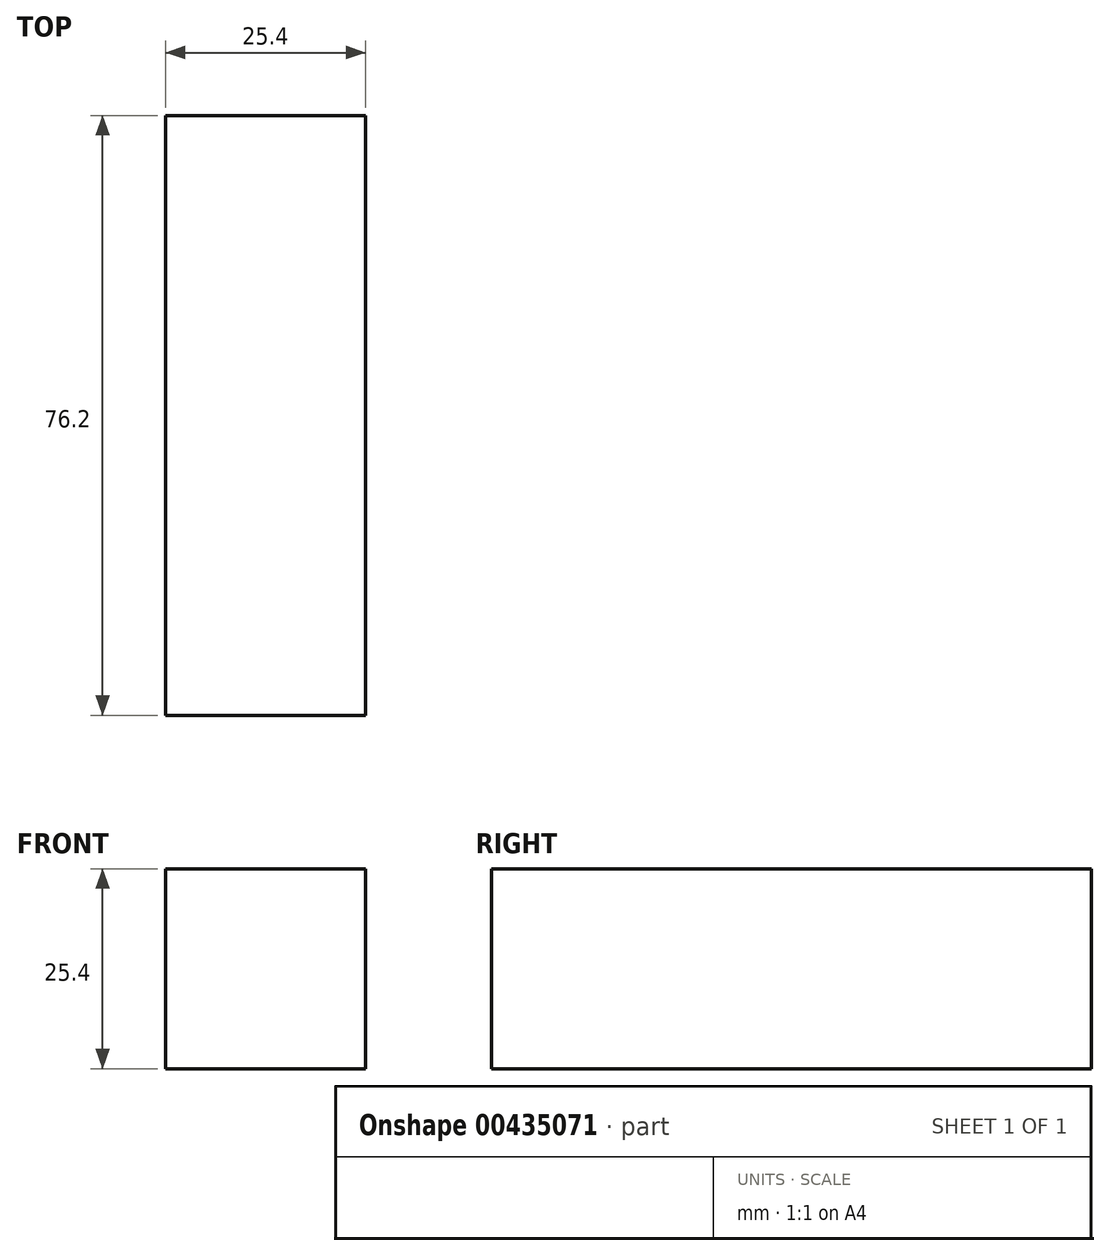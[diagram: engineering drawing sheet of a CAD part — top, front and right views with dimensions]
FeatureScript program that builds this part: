
annotation { "Feature Type Name" : "Feature", "Feature Type Description" : "" }
export const myFeature = defineFeature(function(context is Context, id is Id, definition is map)
    precondition{}
    {
        {
            var Q0;
            Q0=qCreatedBy(makeId("Front.planeOp"),FACE);
            var sketch = newSketch(context, id + "F0", { "sketchPlane" : qUnion([Q0])});
            skLineSegment(sketch, "E0.bottom", {"start": v(0, 0) * mm, "end": v(25.4, 0) * mm});
            skLineSegment(sketch, "E0.top", {"start": v(0, 25.4) * mm, "end": v(25.4, 25.4) * mm});
            skLineSegment(sketch, "E0.left", {"start": v(0, 0) * mm, "end": v(0, 25.4) * mm});
            skLineSegment(sketch, "E0.right", {"start": v(25.4, 0) * mm, "end": v(25.4, 25.4) * mm});
            skSolve(sketch);
        }
        {
            var Q0;
            Q0 = qSketchRegion(id + "F0", true);
            extrude(context, id + "F1", {"entities" : qUnion([Q0]), "depth" : 76.2 * mm});
        }
    });
